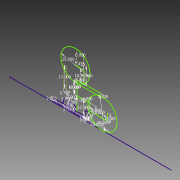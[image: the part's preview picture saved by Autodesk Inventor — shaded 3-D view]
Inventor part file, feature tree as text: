
AUTODESK INVENTOR PART (.ipt)
format: ipt  version: 2014 SP1 (Build 180222100, 222)  size: 95,744 bytes
history: native  units: in
note: dims shown in document units (in); Inventor stores cm internally (conversion verified against a paired STEP export)
features: sketch x1
ambient origin geometry x8: Origin, YZ Plane, XZ Plane, XY Plane, X Axis, Y Axis, Z Axis, Center Point
feature tree (1):
  sketch  "Sketch1"  dims[d0=1.0in d1=27.0in d2=2.0625in d3=1.3125in d4=3.3125in d5=5.125in d6=25.0in d7=6.0in d8=5.0in d9=5.0in d10=12.0in d11=4.0in d13=20.0in d14=15.0in d15=6.0in d16=6.0in d17=7.0in d18=9.0in d19=2.7in d20=11.0in d21=6.0in d22=15.0in d23=6.0in d24=9.0in d25=2.7in d26=10.761in d27=7.438in d28=25.0in d29=17.0in]
